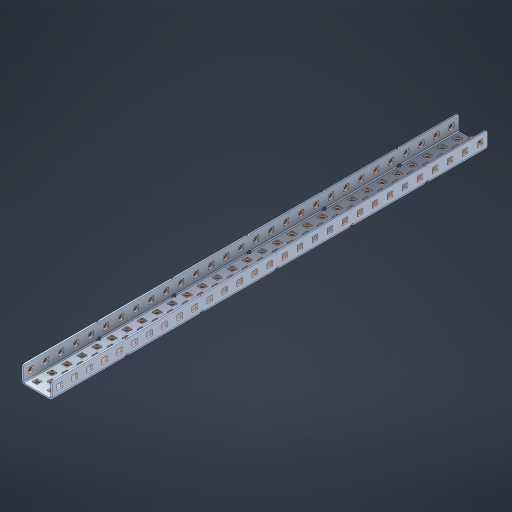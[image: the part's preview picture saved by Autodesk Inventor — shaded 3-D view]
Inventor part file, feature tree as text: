
AUTODESK INVENTOR PART (.ipt)
format: ipt  version: 2023 (Build 270158000, 158)  size: 1,799,680 bytes
history: native  units: in
note: dims shown in document units (in); Inventor stores cm internally (conversion verified against a paired STEP export)
features: other x152, extrude x143, sheet_metal_op x11, sketch x10, pattern_linear x2, mirror x1, chamfer x1
ambient origin geometry x8: Origin, YZ Plane, XZ Plane, XY Plane, X Axis, Y Axis, Z Axis, Center Point
bodies: Solid1 (feature_tree), Body (feature_tree)
feature tree (320):
  sheet_metal_op  "Flanges"
  other  "Flange Pattern Plane"
  other  "Flange Pattern Sketch"
  sheet_metal_op  "Flange Pattern"
  sheet_metal_op  "Body Pattern"
  pattern_linear  "Center Pattern"  Spacing1=0.0469in  [1 undecoded]
  other  "Arc Length"
  mirror  "Notch Mirror"
  pattern_linear  "Notch Pattern"  Spacing1=0.182in  [1 undecoded]
  chamfer  "End Chamfer"
  extrude  "Half Cut"  Depth=0.02in
  sketch  "Sketch1"  dims[d0=1.0in]
  other  "Plate1"
  sketch  "Sketch2"  dims[d1=14.5in]
  other  "Plate2"
  sheet_metal_op  "Bend1"
  sheet_metal_op  "Corner1"
  sketch  "Sketch3"  dims[d2=0.0469in]
  sketch  "Sketch7"  dims[d3=0.0469in]
  other  "Srf1"
  other  "Srf2"
  sketch  "Sketch8"  dims[d4=0.0234in]
  sketch  "Sketch9"  dims[d5=0.0938in]
  other  "Srf91"
  sheet_metal_op  "Body Pattern Sketch"
  other  "Srf92"
  sketch  "Sketch13"  dims[d6=0.0469in]
  sketch  "Sketch14"  dims[d7=0.5in d8=90.0deg d9=0.0312in]
  sketch  "Sketch15"  dims[d10=0.1875in]
  sketch  "Sketch16"  dims[d11=0.0469in d12=0.0469in d16=0.182in d17=0.02in d18=0.0469in d19=0.0in d20=0.25in d21=0.25in d38=11.4173in d40=0.5in d41=0.7874in d43=1.0in d46=0.172in d47=1.0in d48=0.0in d49=0.182in d50=0.02in d51=0.25in d52=0.25in d53=0.0469in d54=0.0in d55=0.172in d56=1.0in d57=0.0in d58=0.25in d60=11.4173in d62=0.5in d63=0.7874in d65=0.5in d85=0.1227in d86=0.1659in d88=0.04in d89=0.0469in d90=0.0in d91=0.04in d92=0.0491in d95=2.5in d96=0.04in d97=0.25in d98=45.0deg d99=0.25in d100=0.5in d101=0.0in d102=2.497in d106=0.182in d107=0.02in d108=0.5in d109=0.5in d110=0.0469in d111=0.0in d112=0.172in d113=0.5in d114=0.0in d117=0.5in d118=0.5in d119=0.5in]
  other  "Srf786"
  other  "Srf823"
  other  "Srf824"
  other  "Srf825"
  other  "Srf826"
  other  "Srf827"
  other  "Srf828"
  other  "Srf829"
  other  "Srf856"
  other  "Srf857"
  other  "Srf858"
  other  "Srf859"
  other  "Srf860"
  other  "Srf861"
  other  "Srf862"
  other  "Srf889"
  other  "Srf890"
  other  "Srf891"
  other  "Srf892"
  other  "Srf893"
  other  "Srf894"
  other  "Srf895"
  other  "Srf896"
  other  "Srf922"
  other  "Srf923"
  other  "Srf924"
  other  "Srf925"
  other  "Srf926"
  other  "Srf959"
  other  "Srf960"
  other  "Srf961"
  other  "Srf962"
  other  "Srf963"
  other  "Srf996"
  other  "Srf997"
  other  "Srf998"
  other  "Srf999"
  other  "Srf1000"
  other  "Srf1143"
  other  "Srf1144"
  other  "Srf1145"
  other  "Srf1146"
  other  "Srf1147"
  other  "Srf1148"
  other  "Srf1149"
  other  "Srf1150"
  other  "Srf1151"
  other  "Srf1152"
  other  "Srf1153"
  other  "Srf1154"
  other  "Srf1155"
  other  "Srf1156"
  other  "Srf1157"
  other  "Srf1158"
  other  "Srf1159"
  other  "Srf1160"
  other  "Srf1161"
  other  "Srf1162"
  other  "Srf1163"
  other  "Srf1164"
  other  "Srf1165"
  other  "Srf1166"
  other  "Srf1167"
  other  "Srf1168"
  other  "Srf1169"
  other  "Srf1170"
  other  "Srf1171"
  other  "Srf1172"
  other  "Srf1173"
  other  "Srf1174"
  other  "Srf1175"
  other  "Srf1176"
  other  "Srf1177"
  other  "Srf1178"
  other  "Srf1179"
  other  "Srf1180"
  other  "Srf1181"
  other  "Srf1182"
  other  "Srf1183"
  other  "Srf1184"
  other  "Srf1185"
  other  "Srf1186"
  other  "Srf1199"
  other  "Srf1200"
  other  "Srf1201"
  other  "Srf1202"
  other  "Srf1203"
  other  "Srf1204"
  other  "Srf1205"
  other  "Srf1206"
  other  "Srf1207"
  other  "Srf1208"
  other  "Srf1209"
  other  "Srf1210"
  other  "Srf1211"
  other  "Srf1212"
  other  "Srf1213"
  other  "Srf1214"
  other  "Srf1215"
  other  "Srf1216"
  other  "Srf1217"
  other  "Srf1218"
  other  "Srf1219"
  other  "Srf1220"
  other  "Srf1221"
  other  "Srf1222"
  other  "Srf1223"
  other  "Srf1224"
  other  "Srf1225"
  other  "Srf1226"
  other  "Srf1227"
  other  "Srf1228"
  other  "Srf1229"
  other  "Srf1230"
  other  "Srf1231"
  other  "Srf1232"
  other  "Srf1233"
  other  "Srf1234"
  other  "Srf1235"
  other  "Srf1236"
  other  "Srf1237"
  other  "Srf1238"
  other  "Srf1239"
  other  "Srf1240"
  other  "Srf1241"
  other  "Srf1242"
  other  "Srf1255"
  other  "Srf1256"
  other  "Srf1257"
  other  "Srf1258"
  other  "Srf1259"
  other  "Srf1260"
  other  "Srf1261"
  other  "Srf1262"
  other  "Srf1263"
  other  "Srf1264"
  other  "Srf1265"
  other  "Srf1266"
  other  "Srf1267"
  other  "Srf1268"
  other  "Srf1269"
  sheet_metal_op  "Flange Stamp"
  sheet_metal_op  "Flange Circle"
  sheet_metal_op  "Body Stamp"
  sheet_metal_op  "Body Circle"
  other  "Center Stamp"
  other  "Center Circle"
  sheet_metal_op  "Notch"
  extrude  "ExtrusionSrf2"  Depth=0.0469in
  extrude  "ExtrusionSrf92"  TaperAngle=0.0deg  [1 undecoded]
  extrude  "ExtrusionSrf823"  Depth=0.5in
  extrude  "ExtrusionSrf824"  Depth=0.5in
  extrude  "ExtrusionSrf825"  Depth=0.5in
  extrude  "ExtrusionSrf826"  Depth=0.5in
  extrude  "ExtrusionSrf827"  Depth=1.0in TaperAngle=0.0deg
  extrude  "ExtrusionSrf828"  Depth=0.5in
  extrude  "ExtrusionSrf829"  Depth=0.02in
  extrude  "ExtrusionSrf856"  Depth=0.5in
  extrude  "ExtrusionSrf857"  Depth=0.5in
  extrude  "ExtrusionSrf858"  Depth=0.0469in
  extrude  "ExtrusionSrf859"  TaperAngle=0.0deg  [1 undecoded]
  extrude  "ExtrusionSrf860"  Depth=0.5in
  extrude  "ExtrusionSrf861"  Depth=1.0in TaperAngle=0.0deg
  extrude  "ExtrusionSrf862"  Depth=0.5in
  extrude  "ExtrusionSrf889"  Depth=0.5in
  extrude  "ExtrusionSrf890"  Depth=0.5in
  extrude  "ExtrusionSrf891"  Depth=0.5in
  extrude  "ExtrusionSrf892"  Depth=0.5in
  extrude  "ExtrusionSrf893"  Depth=0.5in
  extrude  "ExtrusionSrf894"  Depth=0.0469in
  extrude  "ExtrusionSrf895"  TaperAngle=0.0deg  [1 undecoded]
  extrude  "ExtrusionSrf896"  Depth=0.5in
  extrude  "ExtrusionSrf922"  Depth=0.5in
  extrude  "ExtrusionSrf923"  Depth=2.5in
  extrude  "ExtrusionSrf924"  Depth=0.5in TaperAngle=45.0deg
  extrude  "ExtrusionSrf925"  Depth=0.5in
  extrude  "ExtrusionSrf926"  Depth=0.5in TaperAngle=0.0deg
  extrude  "ExtrusionSrf959"  Depth=0.5in
  extrude  "ExtrusionSrf960"  Depth=0.5in
  extrude  "ExtrusionSrf961"  Depth=0.02in
  extrude  "ExtrusionSrf962"  Depth=0.5in
  extrude  "ExtrusionSrf963"  Depth=0.5in
  extrude  "ExtrusionSrf996"  Depth=0.0469in
  extrude  "ExtrusionSrf997"  TaperAngle=0.0deg  [1 undecoded]
  extrude  "ExtrusionSrf998"  Depth=0.5in
  extrude  "ExtrusionSrf999"  Depth=0.5in TaperAngle=0.0deg
  extrude  "ExtrusionSrf1000"  Depth=0.5in
  extrude  "ExtrusionSrf1143"  Depth=0.5in
  extrude  "ExtrusionSrf1144"  Depth=0.5in
  extrude  "ExtrusionSrf1145"  [1 undecoded]
  extrude  "ExtrusionSrf1146"  [1 undecoded]
  extrude  "ExtrusionSrf1147"  [1 undecoded]
  extrude  "ExtrusionSrf1148"  [1 undecoded]
  extrude  "ExtrusionSrf1149"  [1 undecoded]
  extrude  "ExtrusionSrf1150"  [1 undecoded]
  extrude  "ExtrusionSrf1151"  [1 undecoded]
  extrude  "ExtrusionSrf1152"  [1 undecoded]
  extrude  "ExtrusionSrf1153"  [1 undecoded]
  extrude  "ExtrusionSrf1154"  [1 undecoded]
  extrude  "ExtrusionSrf1155"  [1 undecoded]
  extrude  "ExtrusionSrf1156"  [1 undecoded]
  extrude  "ExtrusionSrf1157"  [1 undecoded]
  extrude  "ExtrusionSrf1158"  [1 undecoded]
  extrude  "ExtrusionSrf1159"  [1 undecoded]
  extrude  "ExtrusionSrf1160"  [1 undecoded]
  extrude  "ExtrusionSrf1161"  [1 undecoded]
  extrude  "ExtrusionSrf1162"  [1 undecoded]
  extrude  "ExtrusionSrf1163"  [1 undecoded]
  extrude  "ExtrusionSrf1164"  [1 undecoded]
  extrude  "ExtrusionSrf1165"  [1 undecoded]
  extrude  "ExtrusionSrf1166"  [1 undecoded]
  extrude  "ExtrusionSrf1167"  [1 undecoded]
  extrude  "ExtrusionSrf1168"  [1 undecoded]
  extrude  "ExtrusionSrf1169"  [1 undecoded]
  extrude  "ExtrusionSrf1170"  [1 undecoded]
  extrude  "ExtrusionSrf1171"  [1 undecoded]
  extrude  "ExtrusionSrf1172"  [1 undecoded]
  extrude  "ExtrusionSrf1173"  [1 undecoded]
  extrude  "ExtrusionSrf1174"  [1 undecoded]
  extrude  "ExtrusionSrf1175"  [1 undecoded]
  extrude  "ExtrusionSrf1176"  [1 undecoded]
  extrude  "ExtrusionSrf1177"  [1 undecoded]
  extrude  "ExtrusionSrf1178"  [1 undecoded]
  extrude  "ExtrusionSrf1179"  [1 undecoded]
  extrude  "ExtrusionSrf1180"  [1 undecoded]
  extrude  "ExtrusionSrf1181"  [1 undecoded]
  extrude  "ExtrusionSrf1182"  [1 undecoded]
  extrude  "ExtrusionSrf1183"  [1 undecoded]
  extrude  "ExtrusionSrf1184"  [1 undecoded]
  extrude  "ExtrusionSrf1185"  [1 undecoded]
  extrude  "ExtrusionSrf1186"  [1 undecoded]
  extrude  "ExtrusionSrf1199"  [1 undecoded]
  extrude  "ExtrusionSrf1200"  [1 undecoded]
  extrude  "ExtrusionSrf1201"  [1 undecoded]
  extrude  "ExtrusionSrf1202"  [1 undecoded]
  extrude  "ExtrusionSrf1203"  [1 undecoded]
  extrude  "ExtrusionSrf1204"  [1 undecoded]
  extrude  "ExtrusionSrf1205"  [1 undecoded]
  extrude  "ExtrusionSrf1206"  [1 undecoded]
  extrude  "ExtrusionSrf1207"  [1 undecoded]
  extrude  "ExtrusionSrf1208"  [1 undecoded]
  extrude  "ExtrusionSrf1209"  [1 undecoded]
  extrude  "ExtrusionSrf1210"  [1 undecoded]
  extrude  "ExtrusionSrf1211"  [1 undecoded]
  extrude  "ExtrusionSrf1212"  [1 undecoded]
  extrude  "ExtrusionSrf1213"  [1 undecoded]
  extrude  "ExtrusionSrf1214"  [1 undecoded]
  extrude  "ExtrusionSrf1215"  [1 undecoded]
  extrude  "ExtrusionSrf1216"  [1 undecoded]
  extrude  "ExtrusionSrf1217"  [1 undecoded]
  extrude  "ExtrusionSrf1218"  [1 undecoded]
  extrude  "ExtrusionSrf1219"  [1 undecoded]
  extrude  "ExtrusionSrf1220"  [1 undecoded]
  extrude  "ExtrusionSrf1221"  [1 undecoded]
  extrude  "ExtrusionSrf1222"  [1 undecoded]
  extrude  "ExtrusionSrf1223"  [1 undecoded]
  extrude  "ExtrusionSrf1224"  [1 undecoded]
  extrude  "ExtrusionSrf1225"  [1 undecoded]
  extrude  "ExtrusionSrf1226"  [1 undecoded]
  extrude  "ExtrusionSrf1227"  [1 undecoded]
  extrude  "ExtrusionSrf1228"  [1 undecoded]
  extrude  "ExtrusionSrf1229"  [1 undecoded]
  extrude  "ExtrusionSrf1230"  [1 undecoded]
  extrude  "ExtrusionSrf1231"  [1 undecoded]
  extrude  "ExtrusionSrf1232"  [1 undecoded]
  extrude  "ExtrusionSrf1233"  [1 undecoded]
  extrude  "ExtrusionSrf1234"  [1 undecoded]
  extrude  "ExtrusionSrf1235"  [1 undecoded]
  extrude  "ExtrusionSrf1236"  [1 undecoded]
  extrude  "ExtrusionSrf1237"  [1 undecoded]
  extrude  "ExtrusionSrf1238"  [1 undecoded]
  extrude  "ExtrusionSrf1239"  [1 undecoded]
  extrude  "ExtrusionSrf1240"  [1 undecoded]
  extrude  "ExtrusionSrf1241"  [1 undecoded]
  extrude  "ExtrusionSrf1242"  [1 undecoded]
  extrude  "ExtrusionSrf1255"  [1 undecoded]
  extrude  "ExtrusionSrf1256"  [1 undecoded]
  extrude  "ExtrusionSrf1257"  [1 undecoded]
  extrude  "ExtrusionSrf1258"  [1 undecoded]
  extrude  "ExtrusionSrf1259"  [1 undecoded]
  extrude  "ExtrusionSrf1260"  [1 undecoded]
  extrude  "ExtrusionSrf1261"  [1 undecoded]
  extrude  "ExtrusionSrf1262"  [1 undecoded]
  extrude  "ExtrusionSrf1263"  [1 undecoded]
  extrude  "ExtrusionSrf1264"  [1 undecoded]
  extrude  "ExtrusionSrf1265"  [1 undecoded]
  extrude  "ExtrusionSrf1266"  [1 undecoded]
  extrude  "ExtrusionSrf1267"  [1 undecoded]
  extrude  "ExtrusionSrf1268"  [1 undecoded]
  extrude  "ExtrusionSrf1269"  [1 undecoded]
note: 107 required parameter values undecoded (feature->parameter linkage not recoverable at this tier; creation-order binding heuristic only, values carry confidence <= 0.55)
